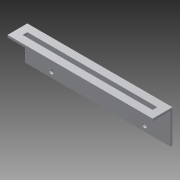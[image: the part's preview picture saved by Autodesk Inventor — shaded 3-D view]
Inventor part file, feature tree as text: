
AUTODESK INVENTOR PART (.ipt)
format: ipt  version: 2015 (Build 190159000, 159)  size: 134,144 bytes
history: native  units: mm
features: sketch x4, extrude x3, other x1, hole x1
ambient origin geometry x8: Origin, YZ Plane, XZ Plane, XY Plane, X Axis, Y Axis, Z Axis, Center Point
bodies: Body1 (feature_tree)
feature tree (9):
  other  "ソリッド1"
  extrude  "押し出し1"  Depth=11.5mm
  extrude  "押し出し2"  Depth=95.0mm
  extrude  "押し出し3"  Depth=1.5mm TaperAngle=0.0deg
  hole  "穴1"  [1 undecoded]
  sketch  "スケッチ1"
  sketch  "スケッチ2"
  sketch  "スケッチ3"
  sketch  "スケッチ4"
note: 1 required parameter value undecoded (feature->parameter linkage not recoverable at this tier; creation-order binding heuristic only, values carry confidence <= 0.55)
